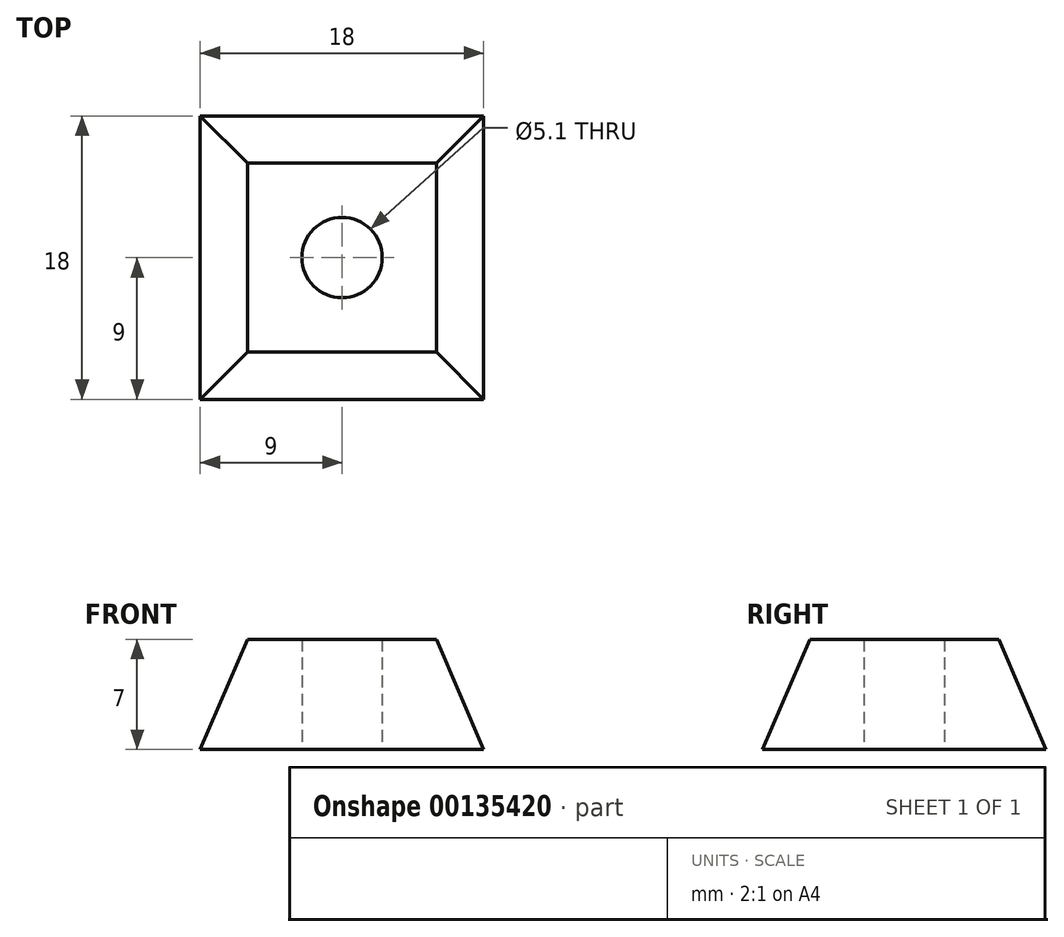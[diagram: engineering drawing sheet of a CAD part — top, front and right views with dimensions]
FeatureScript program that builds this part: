
annotation { "Feature Type Name" : "Feature", "Feature Type Description" : "" }
export const myFeature = defineFeature(function(context is Context, id is Id, definition is map)
    precondition{}
    {
        {
            var Q0;
            Q0=qCreatedBy(makeId("Top.planeOp"),FACE);
            var sketch = newSketch(context, id + "F0", { "sketchPlane" : qUnion([Q0])});
            skLineSegment(sketch, "E0.bottom", {"start": v(9, 9) * mm, "end": v(-9, 9) * mm});
            skLineSegment(sketch, "E0.top", {"start": v(9, -9) * mm, "end": v(-9, -9) * mm});
            skLineSegment(sketch, "E0.left", {"start": v(9, 9) * mm, "end": v(9, -9) * mm});
            skLineSegment(sketch, "E0.right", {"start": v(-9, 9) * mm, "end": v(-9, -9) * mm});
            skPoint(sketch, "E0.middle", {"position": v(0, 0) * mm});
            skSolve(sketch);
        }
        {
            var Q0;
            Q0=makeQuery(id+"F0.imprint","IMPRINT",FACE,{"disambiguationData":[TD([[makeQuery(id+"F0.imprint","IMPRINT",EDGE,{"derivedFrom":sQuery(id+"F0.wireOp",EDGE,"E0.bottom")}),1.0]])]});
            extrude(context, id + "F1", {"entities" : qUnion([Q0]), "depth" : 7 * mm});
        }
        {
            var Q0;
            Q0=makeQuery(id+"F1.opExtrude","CAP_EDGE",EDGE,{"disambiguationData":[OSD([sQuery(id+"F0.wireOp",EDGE,"E0.right")])],"isStart":false});
            var Q1;
            Q1=makeQuery(id+"F1.opExtrude","CAP_EDGE",EDGE,{"disambiguationData":[OSD([sQuery(id+"F0.wireOp",EDGE,"E0.bottom")])],"isStart":false});
            var Q2;
            Q2=makeQuery(id+"F1.opExtrude","CAP_EDGE",EDGE,{"disambiguationData":[OSD([sQuery(id+"F0.wireOp",EDGE,"E0.left")])],"isStart":false});
            var Q3;
            Q3=makeQuery(id+"F1.opExtrude","CAP_EDGE",EDGE,{"disambiguationData":[OSD([sQuery(id+"F0.wireOp",EDGE,"E0.top")])],"isStart":false});
            chamfer(context, id + "F2", {"entities" : qUnion([Q0, Q1, Q2, Q3]), "chamferType" : ChamferType.TWO_OFFSETS, "width1" : 3 * mm, "oppositeDirection" : false, "width2" : 7 * mm, "tangentPropagation" : true});
        }
        {
            var Q0;
            Q0=qCreatedBy(makeId("Top.planeOp"),FACE);
            var sketch = newSketch(context, id + "F3", { "sketchPlane" : qUnion([Q0])});
            skCircle(sketch, "E1", {"center": v(0, 0) * mm, "radius": 2.55 * mm});
            skSolve(sketch);
        }
        {
            var Q0;
            Q0=makeQuery(id+"F3.imprint","IMPRINT",FACE,{"disambiguationData":[TD([[makeQuery(id+"F3.imprint","IMPRINT",EDGE,{"derivedFrom":sQuery(id+"F3.wireOp",EDGE,"E1")}),1.0]])]});
            extrude(context, id + "F4", {"entities" : qUnion([Q0]), "operationType" : NewBodyOperationType.REMOVE, "depth" : 25 * mm});
        }
    });
